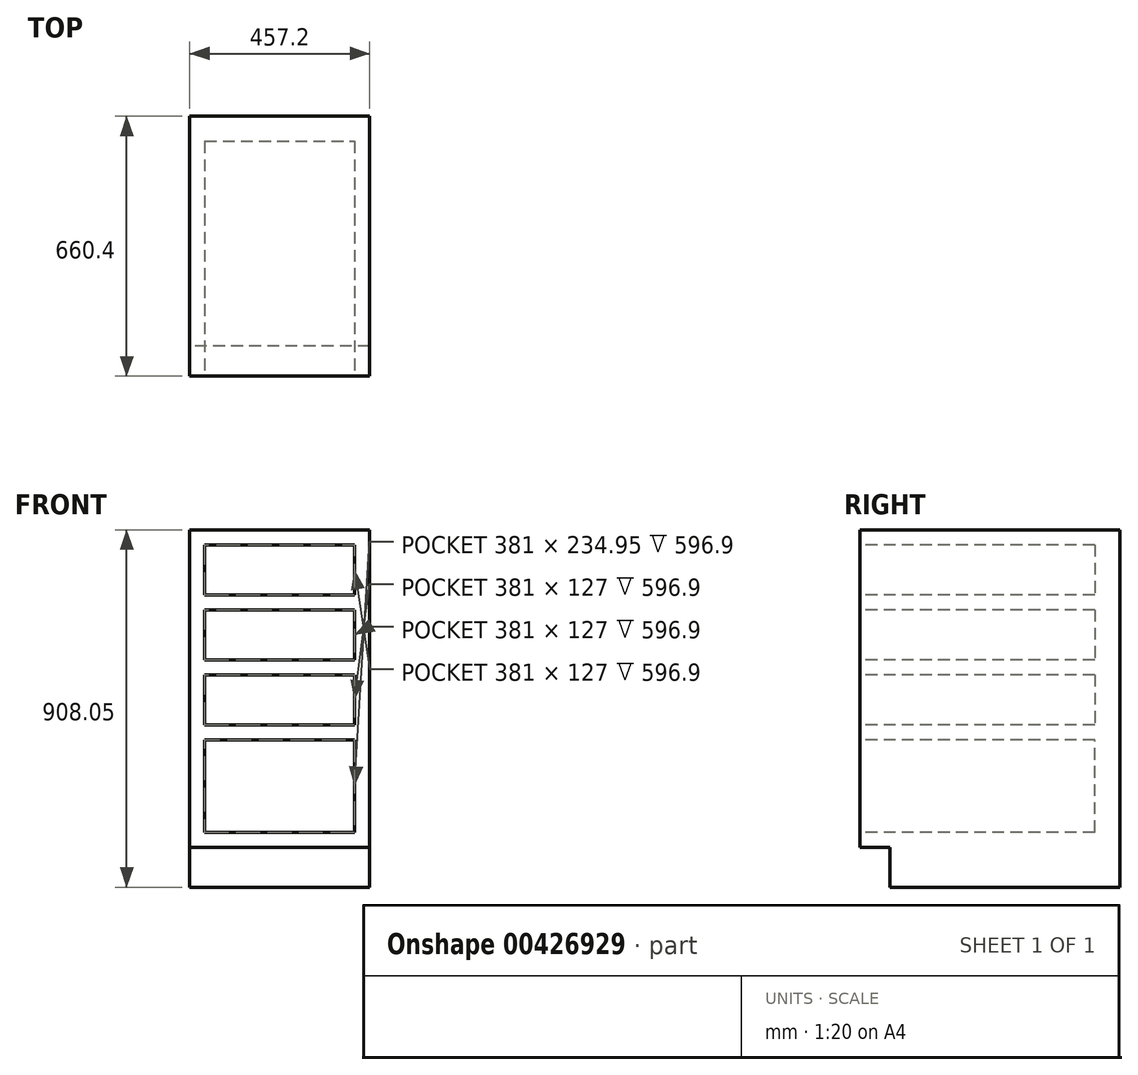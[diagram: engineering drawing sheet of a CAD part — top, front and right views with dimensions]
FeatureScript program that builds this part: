
annotation { "Feature Type Name" : "Feature", "Feature Type Description" : "" }
export const myFeature = defineFeature(function(context is Context, id is Id, definition is map)
    precondition{}
    {
        {
            var Q0;
            Q0=qCreatedBy(makeId("Right.planeOp"),FACE);
            var sketch = newSketch(context, id + "F0", { "sketchPlane" : qUnion([Q0])});
            skLineSegment(sketch, "E0", {"start": v(0, 0) * mm, "end": v(-584.2, 0) * mm});
            skLineSegment(sketch, "E1", {"start": v(-584.2, 0) * mm, "end": v(-584.2, 101.6) * mm});
            skLineSegment(sketch, "E2", {"start": v(-584.2, 101.6) * mm, "end": v(-660.4, 101.6) * mm});
            skLineSegment(sketch, "E3", {"start": v(-660.4, 101.6) * mm, "end": v(-660.4, 908.05) * mm});
            skLineSegment(sketch, "E4", {"start": v(-660.4, 908.05) * mm, "end": v(0, 908.05) * mm});
            skLineSegment(sketch, "E5", {"start": v(0, 908.05) * mm, "end": v(0, 0) * mm});
            skSolve(sketch);
        }
        {
            var Q0;
            Q0=makeQuery(id+"F0.imprint","IMPRINT",FACE,{"disambiguationData":[TD([[makeQuery(id+"F0.imprint","IMPRINT",EDGE,{"derivedFrom":sQuery(id+"F0.wireOp",EDGE,"E0")}),-1.0]])]});
            extrude(context, id + "F1", {"entities" : qUnion([Q0]), "depth" : 457.2 * mm});
        }
        {
            var Q0;
            Q0=makeQuery(id+"F1.opExtrude","SWEPT_FACE",FACE,{"disambiguationData":[OSD([sQuery(id+"F0.wireOp",EDGE,"E3")])]});
            var sketch = newSketch(context, id + "F2", { "sketchPlane" : qUnion([Q0])});
            skLineSegment(sketch, "E6.bottom", {"start": v(38.1, 869.95) * mm, "end": v(419.1, 869.95) * mm});
            skLineSegment(sketch, "E6.top", {"start": v(38.1, 742.95) * mm, "end": v(419.1, 742.95) * mm});
            skLineSegment(sketch, "E6.left", {"start": v(38.1, 869.95) * mm, "end": v(38.1, 742.95) * mm});
            skLineSegment(sketch, "E6.right", {"start": v(419.1, 869.95) * mm, "end": v(419.1, 742.95) * mm});
            skLineSegment(sketch, "E7.bottom", {"start": v(38.1, 704.85) * mm, "end": v(419.1, 704.85) * mm});
            skLineSegment(sketch, "E7.top", {"start": v(38.1, 577.85) * mm, "end": v(419.1, 577.85) * mm});
            skLineSegment(sketch, "E7.left", {"start": v(38.1, 704.85) * mm, "end": v(38.1, 577.85) * mm});
            skLineSegment(sketch, "E7.right", {"start": v(419.1, 704.85) * mm, "end": v(419.1, 577.85) * mm});
            skLineSegment(sketch, "E8.bottom", {"start": v(38.1, 539.75) * mm, "end": v(419.1, 539.75) * mm});
            skLineSegment(sketch, "E8.top", {"start": v(38.1, 412.75) * mm, "end": v(419.1, 412.75) * mm});
            skLineSegment(sketch, "E8.left", {"start": v(38.1, 539.75) * mm, "end": v(38.1, 412.75) * mm});
            skLineSegment(sketch, "E8.right", {"start": v(419.1, 539.75) * mm, "end": v(419.1, 412.75) * mm});
            skLineSegment(sketch, "E9.bottom", {"start": v(38.1, 139.7) * mm, "end": v(419.1, 139.7) * mm});
            skLineSegment(sketch, "E9.top", {"start": v(38.1, 374.65) * mm, "end": v(419.1, 374.65) * mm});
            skLineSegment(sketch, "E9.left", {"start": v(38.1, 139.7) * mm, "end": v(38.1, 374.65) * mm});
            skLineSegment(sketch, "E9.right", {"start": v(419.1, 139.7) * mm, "end": v(419.1, 374.65) * mm});
            skSolve(sketch);
        }
        {
            var Q0;
            Q0=makeQuery(id+"F2.imprint","IMPRINT",FACE,{"disambiguationData":[TD([[makeQuery(id+"F2.imprint","IMPRINT",EDGE,{"derivedFrom":sQuery(id+"F2.wireOp",EDGE,"E6.bottom")}),-1.0]])]});
            var Q1;
            Q1=makeQuery(id+"F2.imprint","IMPRINT",FACE,{"disambiguationData":[TD([[makeQuery(id+"F2.imprint","IMPRINT",EDGE,{"derivedFrom":sQuery(id+"F2.wireOp",EDGE,"E7.bottom")}),-1.0]])]});
            var Q2;
            Q2=makeQuery(id+"F2.imprint","IMPRINT",FACE,{"disambiguationData":[TD([[makeQuery(id+"F2.imprint","IMPRINT",EDGE,{"derivedFrom":sQuery(id+"F2.wireOp",EDGE,"E8.bottom")}),-1.0]])]});
            var Q3;
            Q3=makeQuery(id+"F2.imprint","IMPRINT",FACE,{"disambiguationData":[TD([[makeQuery(id+"F2.imprint","IMPRINT",EDGE,{"derivedFrom":sQuery(id+"F2.wireOp",EDGE,"z5dql7AH-9pPf-yf0r-Lgpp-hoX97IjUhxXj.bottom")}),-1.0]])]});
            var Q4;
            Q4=makeQuery(id+"F2.imprint","IMPRINT",FACE,{"disambiguationData":[TD([[makeQuery(id+"F2.imprint","IMPRINT",EDGE,{"derivedFrom":sQuery(id+"F2.wireOp",EDGE,"E9.bottom")}),1.0]])]});
            extrude(context, id + "F3", {"entities" : qUnion([Q0, Q1, Q2, Q3, Q4]), "operationType" : NewBodyOperationType.REMOVE, "oppositeDirection" : true, "depth" : 596.9 * mm});
        }
    });
